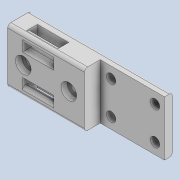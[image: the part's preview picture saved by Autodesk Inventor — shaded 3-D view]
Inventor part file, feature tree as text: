
AUTODESK INVENTOR PART (.ipt)
format: ipt  version: 2020 (Build 240168000, 168)  size: 216,576 bytes
history: native  units: mm
features: sketch x5, extrude x2, fillet x2, plane x1, sweep x1, mirror x1, hole x1
ambient origin geometry x8: Origin, YZ Plane, XZ Plane, XY Plane, X Axis, Y Axis, Z Axis, Center Point
bodies: Solid1 (feature_tree)
feature tree (13):
  extrude  "Extrusion1"  Depth=90.0mm
  extrude  "Extrusion2"  Depth=28.0mm
  plane  "Work Plane1"
  sweep  "Sweep1"
  mirror  "Mirror1"
  fillet  "Fillet1"  Radius=5.0mm
  hole  "Hole1"  [1 undecoded]
  fillet  "Fillet2"  [1 undecoded]
  sketch  "Sketch1"  dims[d0=35.0mm d1=90.0mm]
  sketch  "Sketch2"  dims[d2=21.0mm d3=28.0mm]
  sketch  "Sketch3"  dims[d5=6.0mm d6=6.0mm d7=5.0mm d8=0.0mm]
  sketch  "Sketch4"  dims[d9=7.0mm d10=10.0mm d11=0.0mm d12=-19.5mm]
  sketch  "Sketch6"  dims[d13=8.0mm d14=8.0mm d18=0.0mm d19=0.0mm d20=2.0mm d23=10.0mm d25=10.0mm d26=5.0mm d27=6.0mm d28=10.0mm d29=4.0mm d30=90.0deg d31=8.0mm d32=20.594885mm d33=2.0mm d34=5.0mm d35=20.0mm d36=2.0mm]
note: 2 required parameter values undecoded (feature->parameter linkage not recoverable at this tier; creation-order binding heuristic only, values carry confidence <= 0.55)
